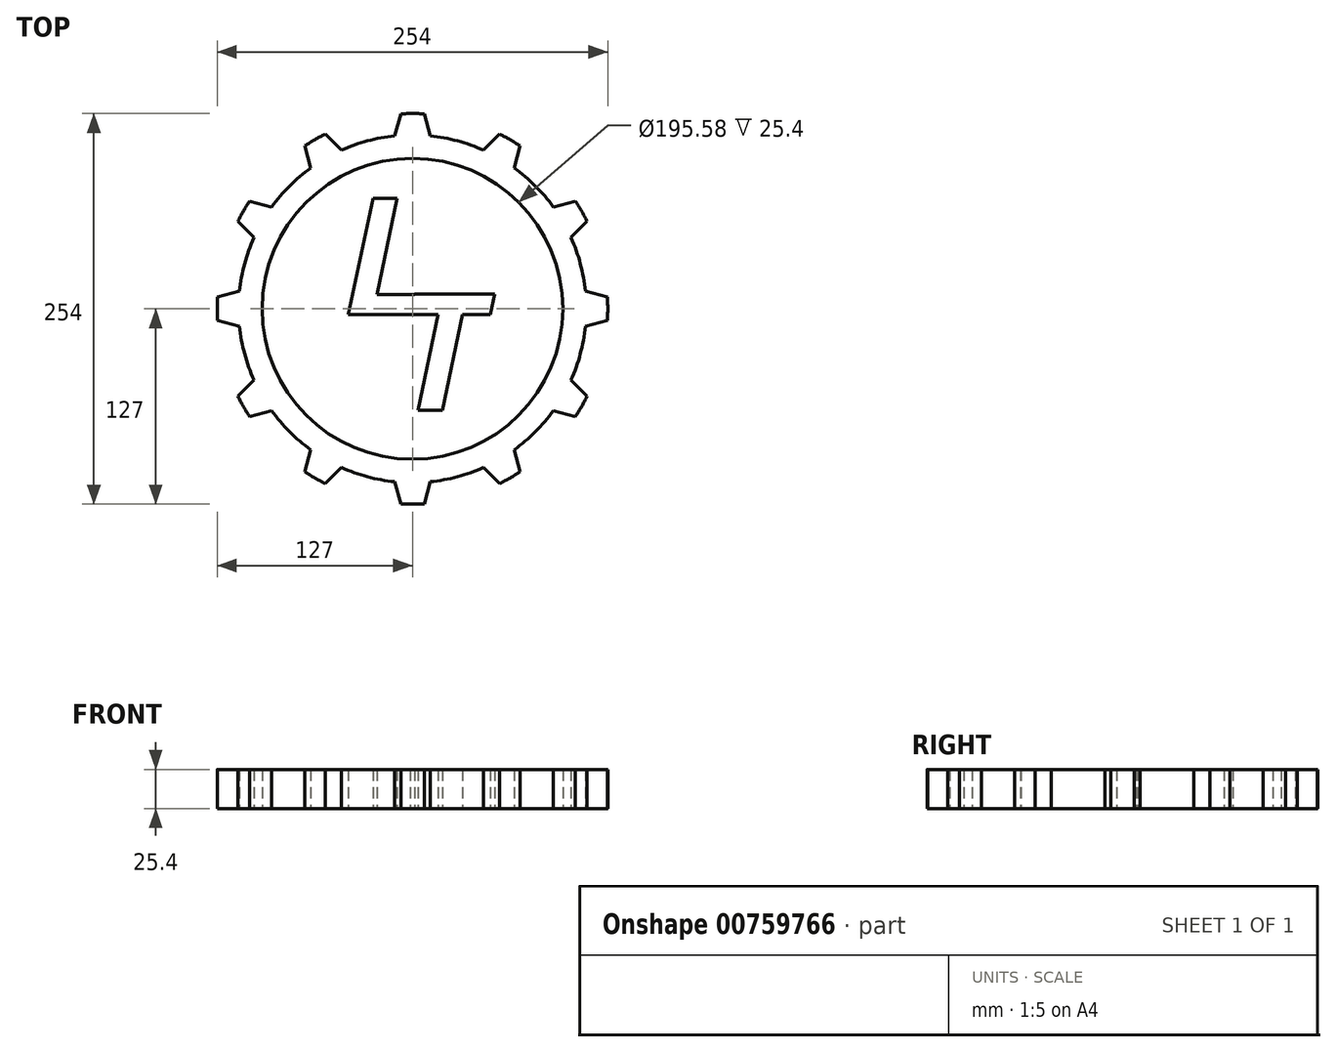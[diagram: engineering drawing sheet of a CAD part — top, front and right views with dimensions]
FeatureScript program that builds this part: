
annotation { "Feature Type Name" : "Feature", "Feature Type Description" : "" }
export const myFeature = defineFeature(function(context is Context, id is Id, definition is map)
    precondition{}
    {
        {
            var Q0;
            Q0=qCreatedBy(makeId("Top.planeOp"),FACE);
            var sketch = newSketch(context, id + "F0", { "sketchPlane" : qUnion([Q0])});
            skArc(sketch, "E0", {"start": v(7.62, 126.77) * mm, "mid": v(0, 127) * mm, "end": v(-7.62, 126.77) * mm});
            skCircle(sketch, "E1", {"center": v(0, 0) * mm, "radius": 97.8 * mm});
            skLineSegment(sketch, "E2", {"start": v(0, 0) * mm, "end": v(0, 127) * mm, "construction": true});
            skArc(sketch, "E3", {"start": v(-11.46, 112.45) * mm, "mid": v(0, -113.03) * mm, "end": v(11.46, 112.45) * mm});
            skLineSegment(sketch, "E4", {"start": v(-7.62, 126.77) * mm, "end": v(-11.46, 112.45) * mm});
            skLineSegment(sketch, "E5", {"start": v(7.62, 126.77) * mm, "end": v(11.46, 112.45) * mm});
            skLineSegment(sketch, "E6.1.0", {"start": v(69.98, 105.98) * mm, "end": v(66.15, 91.65) * mm});
            skLineSegment(sketch, "E6.1.1", {"start": v(0, 0) * mm, "end": v(63.5, 109.99) * mm, "construction": true});
            skArc(sketch, "E6.1.2", {"start": v(69.98, 105.98) * mm, "mid": v(63.5, 109.99) * mm, "end": v(56.79, 113.6) * mm});
            skLineSegment(sketch, "E6.1.3", {"start": v(56.79, 113.6) * mm, "end": v(46.3, 103.11) * mm});
            skLineSegment(sketch, "E6.2.0", {"start": v(113.6, 56.79) * mm, "end": v(103.11, 46.3) * mm});
            skLineSegment(sketch, "E6.2.1", {"start": v(0, 0) * mm, "end": v(109.99, 63.5) * mm, "construction": true});
            skArc(sketch, "E6.2.2", {"start": v(113.6, 56.79) * mm, "mid": v(109.99, 63.5) * mm, "end": v(105.98, 69.98) * mm});
            skLineSegment(sketch, "E6.2.3", {"start": v(105.98, 69.98) * mm, "end": v(91.65, 66.15) * mm});
            skLineSegment(sketch, "E6.3.0", {"start": v(126.77, -7.62) * mm, "end": v(112.45, -11.46) * mm});
            skLineSegment(sketch, "E6.3.1", {"start": v(0, 0) * mm, "end": v(127, 0) * mm, "construction": true});
            skArc(sketch, "E6.3.2", {"start": v(126.77, -7.62) * mm, "mid": v(127, 0) * mm, "end": v(126.77, 7.62) * mm});
            skLineSegment(sketch, "E6.3.3", {"start": v(126.77, 7.62) * mm, "end": v(112.45, 11.46) * mm});
            skLineSegment(sketch, "E6.4.0", {"start": v(105.98, -69.98) * mm, "end": v(91.65, -66.15) * mm});
            skLineSegment(sketch, "E6.4.1", {"start": v(0, 0) * mm, "end": v(109.99, -63.5) * mm, "construction": true});
            skArc(sketch, "E6.4.2", {"start": v(105.98, -69.98) * mm, "mid": v(109.99, -63.5) * mm, "end": v(113.6, -56.79) * mm});
            skLineSegment(sketch, "E6.4.3", {"start": v(113.6, -56.79) * mm, "end": v(103.11, -46.3) * mm});
            skLineSegment(sketch, "E6.5.0", {"start": v(56.79, -113.6) * mm, "end": v(46.3, -103.11) * mm});
            skLineSegment(sketch, "E6.5.1", {"start": v(0, 0) * mm, "end": v(63.5, -109.99) * mm, "construction": true});
            skArc(sketch, "E6.5.2", {"start": v(56.79, -113.6) * mm, "mid": v(63.5, -109.99) * mm, "end": v(69.98, -105.98) * mm});
            skLineSegment(sketch, "E6.5.3", {"start": v(69.98, -105.98) * mm, "end": v(66.15, -91.65) * mm});
            skLineSegment(sketch, "E6.6.0", {"start": v(-7.62, -126.77) * mm, "end": v(-11.46, -112.45) * mm});
            skLineSegment(sketch, "E6.6.1", {"start": v(0, 0) * mm, "end": v(0, -127) * mm, "construction": true});
            skArc(sketch, "E6.6.2", {"start": v(-7.62, -126.77) * mm, "mid": v(0, -127) * mm, "end": v(7.62, -126.77) * mm});
            skLineSegment(sketch, "E6.6.3", {"start": v(7.62, -126.77) * mm, "end": v(11.46, -112.45) * mm});
            skLineSegment(sketch, "E6.7.0", {"start": v(-69.98, -105.98) * mm, "end": v(-66.15, -91.65) * mm});
            skLineSegment(sketch, "E6.7.1", {"start": v(0, 0) * mm, "end": v(-63.5, -109.99) * mm, "construction": true});
            skArc(sketch, "E6.7.2", {"start": v(-69.98, -105.98) * mm, "mid": v(-63.5, -109.99) * mm, "end": v(-56.79, -113.6) * mm});
            skLineSegment(sketch, "E6.7.3", {"start": v(-56.79, -113.6) * mm, "end": v(-46.3, -103.11) * mm});
            skLineSegment(sketch, "E6.8.0", {"start": v(-113.6, -56.79) * mm, "end": v(-103.11, -46.3) * mm});
            skLineSegment(sketch, "E6.8.1", {"start": v(0, 0) * mm, "end": v(-109.99, -63.5) * mm, "construction": true});
            skArc(sketch, "E6.8.2", {"start": v(-113.6, -56.79) * mm, "mid": v(-109.99, -63.5) * mm, "end": v(-105.98, -69.98) * mm});
            skLineSegment(sketch, "E6.8.3", {"start": v(-105.98, -69.98) * mm, "end": v(-91.65, -66.15) * mm});
            skLineSegment(sketch, "E6.9.0", {"start": v(-126.77, 7.62) * mm, "end": v(-112.45, 11.46) * mm});
            skLineSegment(sketch, "E6.9.1", {"start": v(0, 0) * mm, "end": v(-127, 0) * mm, "construction": true});
            skArc(sketch, "E6.9.2", {"start": v(-126.77, 7.62) * mm, "mid": v(-127, 0) * mm, "end": v(-126.77, -7.62) * mm});
            skLineSegment(sketch, "E6.9.3", {"start": v(-126.77, -7.62) * mm, "end": v(-112.45, -11.46) * mm});
            skLineSegment(sketch, "E6.10.0", {"start": v(-105.98, 69.98) * mm, "end": v(-91.65, 66.15) * mm});
            skLineSegment(sketch, "E6.10.1", {"start": v(0, 0) * mm, "end": v(-109.99, 63.5) * mm, "construction": true});
            skArc(sketch, "E6.10.2", {"start": v(-105.98, 69.98) * mm, "mid": v(-109.99, 63.5) * mm, "end": v(-113.6, 56.79) * mm});
            skLineSegment(sketch, "E6.10.3", {"start": v(-113.6, 56.79) * mm, "end": v(-103.11, 46.3) * mm});
            skLineSegment(sketch, "E6.11.0", {"start": v(-56.79, 113.6) * mm, "end": v(-46.3, 103.11) * mm});
            skLineSegment(sketch, "E6.11.1", {"start": v(0, 0) * mm, "end": v(-63.5, 109.99) * mm, "construction": true});
            skArc(sketch, "E6.11.2", {"start": v(-56.79, 113.6) * mm, "mid": v(-63.5, 109.99) * mm, "end": v(-69.98, 105.98) * mm});
            skLineSegment(sketch, "E6.11.3", {"start": v(-69.98, 105.98) * mm, "end": v(-66.15, 91.65) * mm});
            skLineSegment(sketch, "E6.anchor1", {"start": v(0, 0) * mm, "end": v(-11.46, 112.45) * mm, "construction": true});
            skLineSegment(sketch, "E6.anchor2", {"start": v(0, 0) * mm, "end": v(-66.15, 91.65) * mm, "construction": true});
            skSolve(sketch);
        }
        {
            var Q0;
            Q0 = qSketchRegion(id + "F0", true);
            extrude(context, id + "F1", {"entities" : qUnion([Q0]), "depth" : 25.4 * mm, "offsetDistance" : 25.4 * mm});
        }
        {
            var Q0;
            Q0=qCreatedBy(makeId("Top.planeOp"),FACE);
            var sketch = newSketch(context, id + "F2", { "sketchPlane" : qUnion([Q0])});
            skText(sketch, "E7", { "text": "L", "fontName": "OpenSans-BoldItalic.ttf"});
            skText(sketch, "E8", { "text": "T", "fontName": "OpenSans-BoldItalic.ttf"});
            const initialGuessF2  = {"E7": [-0.04446, -0.00381, 1, 0, 0.0762], "E8": [-0.01016, -0.06604, 1, 0, 0.0762]};
            skSetInitialGuess(sketch, initialGuessF2);
            skSolve(sketch);
        }
        {
            var Q0;
            Q0 = qSketchRegion(id + "F2", true);
            extrude(context, id + "F3", {"entities" : qUnion([Q0]), "depth" : 25.4 * mm, "offsetDistance" : 25.4 * mm});
        }
    });
